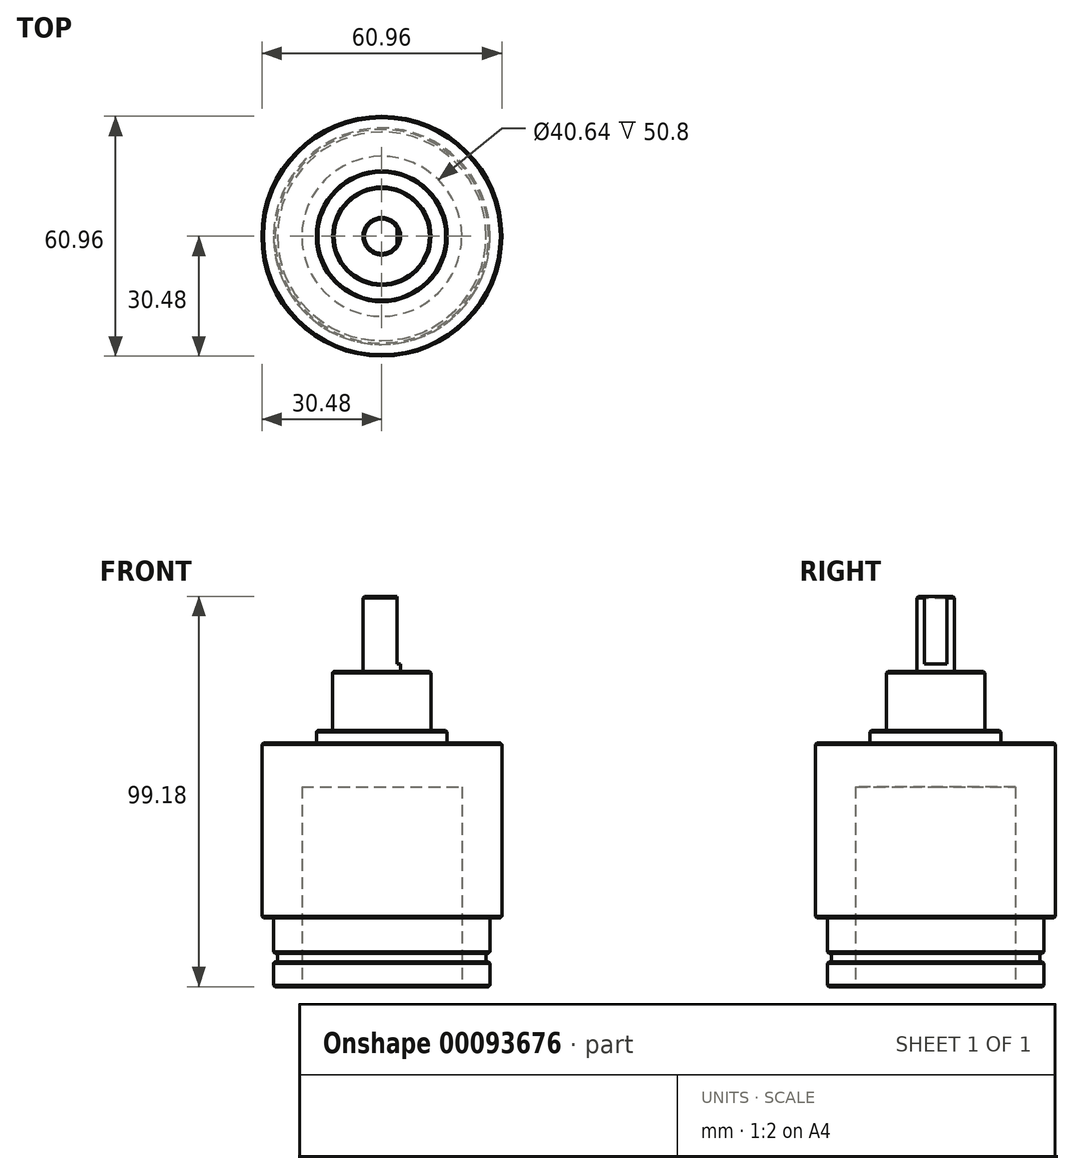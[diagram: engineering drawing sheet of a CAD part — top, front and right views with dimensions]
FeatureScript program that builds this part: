
annotation { "Feature Type Name" : "Feature", "Feature Type Description" : "" }
export const myFeature = defineFeature(function(context is Context, id is Id, definition is map)
    precondition{}
    {
        {
            var Q0;
            Q0=qCreatedBy(makeId("Front.planeOp"),FACE);
            var sketch = newSketch(context, id + "F0", { "sketchPlane" : qUnion([Q0])});
            skLineSegment(sketch, "E0", {"start": v(0, 0) * mm, "end": v(-4.76, 0) * mm});
            skLineSegment(sketch, "E1", {"start": v(-4.76, 0) * mm, "end": v(-4.76, -19.05) * mm});
            skLineSegment(sketch, "E2", {"start": v(-4.76, -19.05) * mm, "end": v(-12.5, -19.05) * mm});
            skLineSegment(sketch, "E3", {"start": v(-12.5, -19.05) * mm, "end": v(-12.5, -34.05) * mm});
            skLineSegment(sketch, "E4", {"start": v(-12.5, -34.05) * mm, "end": v(-16.63, -34.05) * mm});
            skLineSegment(sketch, "E5", {"start": v(-30.48, -81.67) * mm, "end": v(-27.5, -81.67) * mm});
            skLineSegment(sketch, "E6", {"start": v(-27.5, -81.67) * mm, "end": v(-27.5, -90.68) * mm});
            skLineSegment(sketch, "E7", {"start": v(-27.5, -99.17) * mm, "end": v(-20.32, -99.17) * mm});
            skLineSegment(sketch, "E8", {"start": v(0, -48.38) * mm, "end": v(0, 0) * mm});
            skLineSegment(sketch, "E9", {"start": v(-27.5, -90.68) * mm, "end": v(-26.5, -90.68) * mm});
            skLineSegment(sketch, "E10", {"start": v(-26.5, -90.68) * mm, "end": v(-26.5, -92.83) * mm});
            skLineSegment(sketch, "E11", {"start": v(-26.5, -92.83) * mm, "end": v(-27.5, -92.83) * mm});
            skLineSegment(sketch, "E12.trimOffspring", {"start": v(-27.5, -92.83) * mm, "end": v(-27.5, -99.17) * mm});
            skLineSegment(sketch, "E13", {"start": v(-20.32, -99.17) * mm, "end": v(-20.32, -48.38) * mm});
            skLineSegment(sketch, "E14", {"start": v(-20.32, -48.38) * mm, "end": v(0, -48.38) * mm});
            skPoint(sketch, "E15.orphan", {"position": v(0, -99.17) * mm});
            skLineSegment(sketch, "E16", {"start": v(-16.63, -34.05) * mm, "end": v(-16.63, -37.22) * mm});
            skLineSegment(sketch, "E17", {"start": v(-30.48, -81.67) * mm, "end": v(-30.48, -37.22) * mm});
            skLineSegment(sketch, "E18", {"start": v(-30.48, -37.22) * mm, "end": v(-16.63, -37.22) * mm});
            skSolve(sketch);
        }
        {
            var Q0;
            Q0=qSketchRegion(id+"F0",true);
            var Q1;
            Q1=sQuery(id+"F0.wireOp",EDGE,"E8");
            revolve(context, id + "F1", {"entities" : qUnion([Q0]), "axis" : qUnion([Q1]), "revolveType" : RevolveType.FULL});
        }
        {
            var Q0;
            Q0=qCreatedBy(makeId("Right.planeOp"),FACE);
            cPlane(context, id + "F2", {"entities" : qUnion([Q0]), "cplaneType" : CPlaneType.OFFSET, "offset" : 3.8 * mm, "width" : 152.4 * mm, "height" : 152.4 * mm});
        }
        {
            var Q0;
            Q0=qCreatedBy(id+"F2.planeOp",FACE);
            var sketch = newSketch(context, id + "F3", { "sketchPlane" : qUnion([Q0])});
            skLineSegment(sketch, "E19", {"start": v(-4.76, -19.05) * mm, "end": v(-4.76, 0) * mm});
            skLineSegment(sketch, "E20", {"start": v(4.76, 0) * mm, "end": v(4.76, -19.05) * mm});
            skLineSegment(sketch, "E21", {"start": v(4.76, 0) * mm, "end": v(-4.76, 0) * mm});
            skLineSegment(sketch, "E22", {"start": v(-4.76, -17.15) * mm, "end": v(4.76, -17.15) * mm});
            skSolve(sketch);
        }
        {
            var Q0;
            Q0=makeQuery(id+"F3.imprint","IMPRINT",FACE,{"disambiguationData":[TD([[makeQuery(id+"F3.imprint","IMPRINT",EDGE,{"derivedFrom":sQuery(id+"F3.wireOp",EDGE,"E19")}),-1.0]])]});
            extrude(context, id + "F4", {"entities" : qUnion([Q0]), "operationType" : NewBodyOperationType.REMOVE, "endBound" : BoundingType.THROUGH_ALL, "depth" : 25.4 * mm});
        }
        {
            var Q0;
            Q0=makeQuery(id+"F1.opRevolve","SWEPT_EDGE",EDGE,{"disambiguationData":[OSD([sQuery(id+"F0.wireOp",EDGE,"E3"),sQuery(id+"F0.wireOp",EDGE,"E4")])]});
            var Q1;
            Q1=makeQuery(id+"F1.opRevolve","SWEPT_EDGE",EDGE,{"disambiguationData":[OSD([sQuery(id+"F0.wireOp",EDGE,"E16"),sQuery(id+"F0.wireOp",EDGE,"E18")])]});
            var Q2;
            Q2=makeQuery(id+"F1.opRevolve","SWEPT_EDGE",EDGE,{"disambiguationData":[OSD([sQuery(id+"F0.wireOp",EDGE,"E5"),sQuery(id+"F0.wireOp",EDGE,"E6")])]});
            var Q3;
            Q3=makeQuery(id+"F1.opRevolve","SWEPT_EDGE",EDGE,{"disambiguationData":[OSD([sQuery(id+"F0.wireOp",EDGE,"E9"),sQuery(id+"F0.wireOp",EDGE,"E10")])]});
            var Q4;
            Q4=makeQuery(id+"F1.opRevolve","SWEPT_EDGE",EDGE,{"disambiguationData":[OSD([sQuery(id+"F0.wireOp",EDGE,"E10"),sQuery(id+"F0.wireOp",EDGE,"E11")])]});
            var Q5;
            Q5=makeQuery(id+"F1.opRevolve","SWEPT_EDGE",EDGE,{"disambiguationData":[OSD([sQuery(id+"F0.wireOp",EDGE,"E1"),sQuery(id+"F0.wireOp",EDGE,"E2")])]});
            fillet(context, id + "F5", {"entities" : qUnion([Q0, Q1, Q2, Q3, Q4, Q5]), "radius" : 0.38 * mm, "tangentPropagation" : true, "allowEdgeOverflow" : false});
        }
        {
            var Q0;
            Q0=makeQuery(id+"F1.opRevolve","SWEPT_EDGE",EDGE,{"disambiguationData":[OSD([sQuery(id+"F0.wireOp",EDGE,"E2"),sQuery(id+"F0.wireOp",EDGE,"E3")])]});
            var Q1;
            Q1=makeQuery(id+"F1.opRevolve","SWEPT_EDGE",EDGE,{"disambiguationData":[OSD([sQuery(id+"F0.wireOp",EDGE,"E0"),sQuery(id+"F0.wireOp",EDGE,"E1")])]});
            var Q2;
            Q2=makeQuery(id+"F1.opRevolve","SWEPT_EDGE",EDGE,{"disambiguationData":[OSD([sQuery(id+"F0.wireOp",EDGE,"E17"),sQuery(id+"F0.wireOp",EDGE,"E18")])]});
            var Q3;
            Q3=makeQuery(id+"F1.opRevolve","SWEPT_EDGE",EDGE,{"disambiguationData":[OSD([sQuery(id+"F0.wireOp",EDGE,"E5"),sQuery(id+"F0.wireOp",EDGE,"E17")])]});
            var Q4;
            Q4=makeQuery(id+"F1.opRevolve","SWEPT_EDGE",EDGE,{"disambiguationData":[OSD([sQuery(id+"F0.wireOp",EDGE,"E7"),sQuery(id+"F0.wireOp",EDGE,"E12.trimOffspring")])]});
            var Q5;
            Q5=makeQuery(id+"F1.opRevolve","SWEPT_EDGE",EDGE,{"disambiguationData":[OSD([sQuery(id+"F0.wireOp",EDGE,"E6"),sQuery(id+"F0.wireOp",EDGE,"E9")])]});
            var Q6;
            Q6=makeQuery(id+"F1.opRevolve","SWEPT_EDGE",EDGE,{"disambiguationData":[OSD([sQuery(id+"F0.wireOp",EDGE,"E11"),sQuery(id+"F0.wireOp",EDGE,"E12.trimOffspring")])]});
            var Q7;
            Q7=makeQuery(id+"F1.opRevolve","SWEPT_EDGE",EDGE,{"disambiguationData":[OSD([sQuery(id+"F0.wireOp",EDGE,"E4"),sQuery(id+"F0.wireOp",EDGE,"E16")])]});
            chamfer(context, id + "F6", {"entities" : qUnion([Q0, Q1, Q2, Q3, Q4, Q5, Q6, Q7]), "width" : 0.38 * mm, "tangentPropagation" : true});
        }
    });
